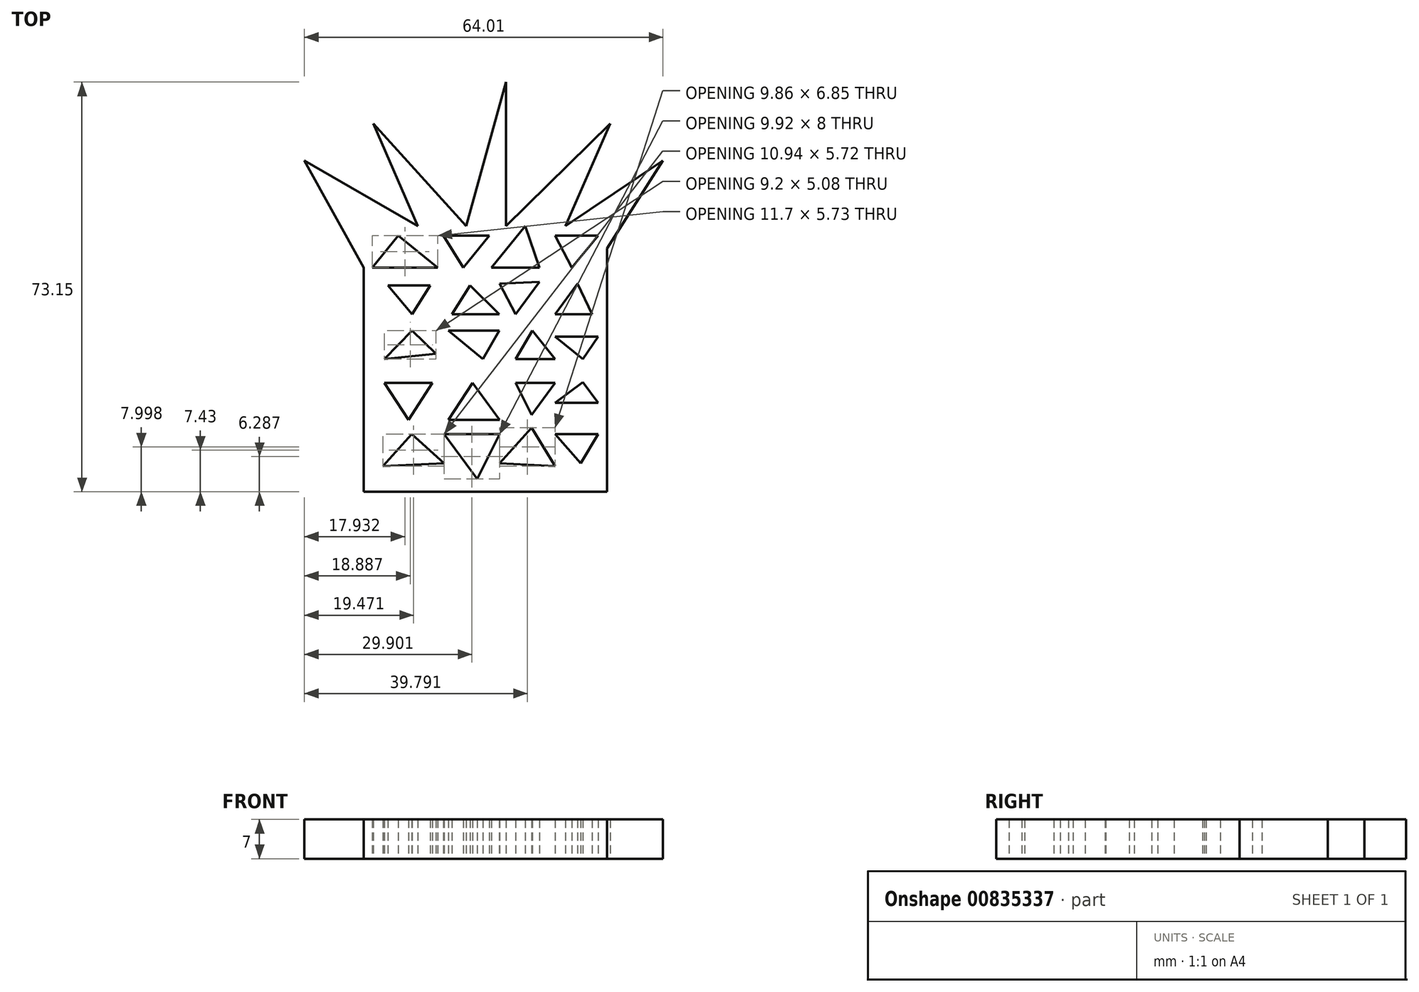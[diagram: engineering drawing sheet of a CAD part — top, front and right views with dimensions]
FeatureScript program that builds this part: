
annotation { "Feature Type Name" : "Feature", "Feature Type Description" : "" }
export const myFeature = defineFeature(function(context is Context, id is Id, definition is map)
    precondition{}
    {
        {
            var Q0;
            Q0=qCreatedBy(makeId("Top.planeOp"),FACE);
            var sketch = newSketch(context, id + "F0", { "sketchPlane" : qUnion([Q0])});
            skLineSegment(sketch, "E0.top", {"start": v(-34.1, -15.86) * mm, "end": v(9.29, -15.86) * mm});
            skLineSegment(sketch, "E0.left", {"start": v(-34.1, 24.13) * mm, "end": v(-34.1, -15.86) * mm});
            skLineSegment(sketch, "E0.right", {"start": v(9.29, 27.44) * mm, "end": v(9.29, -15.86) * mm});
            skLineSegment(sketch, "E1", {"start": v(9.29, 27.57) * mm, "end": v(19.29, 43.3) * mm});
            skLineSegment(sketch, "E2", {"start": v(19.29, 43.3) * mm, "end": v(1.9, 31.58) * mm});
            skLineSegment(sketch, "E3", {"start": v(1.9, 31.58) * mm, "end": v(9.86, 49.86) * mm});
            skLineSegment(sketch, "E4", {"start": v(9.86, 49.86) * mm, "end": v(-8.72, 31.58) * mm});
            skLineSegment(sketch, "E5", {"start": v(-8.72, 31.58) * mm, "end": v(-8.72, 57.3) * mm});
            skLineSegment(sketch, "E6", {"start": v(-8.72, 57.3) * mm, "end": v(-15.87, 31.58) * mm});
            skLineSegment(sketch, "E7", {"start": v(-15.87, 31.58) * mm, "end": v(-32.43, 49.86) * mm});
            skLineSegment(sketch, "E8", {"start": v(-32.43, 49.86) * mm, "end": v(-24.47, 31.58) * mm});
            skLineSegment(sketch, "E9", {"start": v(-24.47, 31.58) * mm, "end": v(-44.72, 43.3) * mm});
            skLineSegment(sketch, "E10", {"start": v(-44.72, 43.3) * mm, "end": v(-34.1, 24.13) * mm});
            skLineSegment(sketch, "E11", {"start": v(-15.87, 31.58) * mm, "end": v(-15.87, 31.58) * mm});
            skLineSegment(sketch, "E12", {"start": v(-32.64, 24.13) * mm, "end": v(-27.99, 29.86) * mm});
            skLineSegment(sketch, "E13", {"start": v(-27.99, 29.86) * mm, "end": v(-20.94, 24.13) * mm});
            skLineSegment(sketch, "E14", {"start": v(-20.94, 24.13) * mm, "end": v(-32.64, 24.13) * mm});
            skLineSegment(sketch, "E15", {"start": v(-19.93, 29.86) * mm, "end": v(-16.37, 24.13) * mm});
            skLineSegment(sketch, "E16", {"start": v(-16.37, 24.13) * mm, "end": v(-11.72, 29.86) * mm});
            skLineSegment(sketch, "E17", {"start": v(-11.72, 29.86) * mm, "end": v(-19.93, 29.86) * mm});
            skLineSegment(sketch, "E18", {"start": v(-11.33, 24.13) * mm, "end": v(-5.29, 31.58) * mm});
            skLineSegment(sketch, "E19", {"start": v(-5.29, 31.58) * mm, "end": v(-2.78, 24.13) * mm});
            skLineSegment(sketch, "E20", {"start": v(-11.33, 24.13) * mm, "end": v(-2.78, 24.13) * mm});
            skLineSegment(sketch, "E21", {"start": v(0, 29.86) * mm, "end": v(3.02, 24.13) * mm});
            skLineSegment(sketch, "E22", {"start": v(-29.8, 20.96) * mm, "end": v(-22.23, 20.96) * mm});
            skLineSegment(sketch, "E23", {"start": v(-22.23, 20.96) * mm, "end": v(-25.48, 15.86) * mm});
            skLineSegment(sketch, "E24", {"start": v(-29.8, 20.96) * mm, "end": v(-25.48, 15.86) * mm});
            skLineSegment(sketch, "E25", {"start": v(-18.4, 15.86) * mm, "end": v(-15.16, 20.96) * mm});
            skLineSegment(sketch, "E26", {"start": v(-15.16, 20.96) * mm, "end": v(-9.94, 15.86) * mm});
            skLineSegment(sketch, "E27", {"start": v(-18.4, 15.86) * mm, "end": v(-9.94, 15.86) * mm});
            skLineSegment(sketch, "E28", {"start": v(-9.86, 21.29) * mm, "end": v(-7, 15.86) * mm});
            skLineSegment(sketch, "E29", {"start": v(-2.78, 21.58) * mm, "end": v(-7, 15.86) * mm});
            skLineSegment(sketch, "E30", {"start": v(-2.78, 21.58) * mm, "end": v(-9.86, 21.29) * mm});
            skLineSegment(sketch, "E31", {"start": v(0, 15.86) * mm, "end": v(4, 21.29) * mm});
            skLineSegment(sketch, "E32", {"start": v(0, 15.86) * mm, "end": v(6.64, 15.86) * mm});
            skPoint(sketch, "E32.endSnap0", {"position": v(6.64, 18.7) * mm});
            skLineSegment(sketch, "E33", {"start": v(-30.43, 7.86) * mm, "end": v(-25.48, 12.93) * mm});
            skPoint(sketch, "E33.startSnap0", {"position": v(-34.1, 7.86) * mm});
            skLineSegment(sketch, "E34", {"start": v(-25.48, 12.93) * mm, "end": v(-21.23, 8.8) * mm});
            skLineSegment(sketch, "E35", {"start": v(-30.43, 7.86) * mm, "end": v(-21.23, 8.8) * mm});
            skLineSegment(sketch, "E36", {"start": v(-19, 12.93) * mm, "end": v(-9.94, 12.93) * mm});
            skLineSegment(sketch, "E37", {"start": v(-9.94, 12.93) * mm, "end": v(-12.87, 7.86) * mm});
            skLineSegment(sketch, "E38", {"start": v(-19, 12.93) * mm, "end": v(-12.87, 7.86) * mm});
            skLineSegment(sketch, "E39", {"start": v(-7, 7.86) * mm, "end": v(-4.06, 12.93) * mm});
            skLineSegment(sketch, "E40", {"start": v(-4.06, 12.93) * mm, "end": v(0, 7.86) * mm});
            skLineSegment(sketch, "E41", {"start": v(-7, 7.86) * mm, "end": v(0, 7.86) * mm});
            skPoint(sketch, "E42.endSnap0", {"position": v(9.29, 7.86) * mm});
            skLineSegment(sketch, "E43", {"start": v(0, 11.86) * mm, "end": v(5, 7.86) * mm});
            skLineSegment(sketch, "E44", {"start": v(-30.43, 3.57) * mm, "end": v(-21.86, 3.57) * mm});
            skLineSegment(sketch, "E45", {"start": v(-21.86, 3.57) * mm, "end": v(-26.15, -3) * mm});
            skLineSegment(sketch, "E46", {"start": v(-30.43, 3.57) * mm, "end": v(-26.15, -3) * mm});
            skLineSegment(sketch, "E47", {"start": v(-19, -3) * mm, "end": v(-14.72, 3.57) * mm});
            skLineSegment(sketch, "E48", {"start": v(-14.72, 3.57) * mm, "end": v(-9.86, -3) * mm});
            skLineSegment(sketch, "E49", {"start": v(-19, -3) * mm, "end": v(-9.86, -3) * mm});
            skLineSegment(sketch, "E50", {"start": v(-7, 3.57) * mm, "end": v(0, 3.57) * mm});
            skLineSegment(sketch, "E51", {"start": v(0, 3.57) * mm, "end": v(-4.14, -2.14) * mm});
            skLineSegment(sketch, "E52", {"start": v(-7, 3.57) * mm, "end": v(-4.14, -2.14) * mm});
            skLineSegment(sketch, "E53", {"start": v(0, 0) * mm, "end": v(5, 3.7) * mm});
            skLineSegment(sketch, "E54", {"start": v(-30.72, -11.29) * mm, "end": v(-25.57, -5.57) * mm});
            skLineSegment(sketch, "E55", {"start": v(-25.57, -5.57) * mm, "end": v(-19.78, -10.79) * mm});
            skLineSegment(sketch, "E56", {"start": v(-30.72, -11.29) * mm, "end": v(-19.78, -10.79) * mm});
            skLineSegment(sketch, "E57", {"start": v(-19.78, -5.57) * mm, "end": v(-9.86, -5.57) * mm});
            skLineSegment(sketch, "E58", {"start": v(-9.86, -5.57) * mm, "end": v(-13.86, -13.57) * mm});
            skLineSegment(sketch, "E59", {"start": v(-19.78, -5.57) * mm, "end": v(-13.86, -13.57) * mm});
            skLineSegment(sketch, "E60", {"start": v(-9.86, -10.79) * mm, "end": v(-4.14, -4.44) * mm});
            skLineSegment(sketch, "E61", {"start": v(-4.14, -4.44) * mm, "end": v(0, -11.29) * mm});
            skLineSegment(sketch, "E62", {"start": v(-9.86, -10.79) * mm, "end": v(0, -11.29) * mm});
            skLineSegment(sketch, "E63", {"start": v(4.6, -10.79) * mm, "end": v(0, -5.57) * mm});
            skLineSegment(sketch, "E64", {"start": v(5, 3.7) * mm, "end": v(7.73, 0) * mm});
            skLineSegment(sketch, "E65", {"start": v(7.73, 0) * mm, "end": v(0, 0) * mm});
            skLineSegment(sketch, "E66", {"start": v(0, -5.57) * mm, "end": v(7.73, -5.57) * mm});
            skLineSegment(sketch, "E67", {"start": v(7.73, -5.57) * mm, "end": v(4.6, -10.79) * mm});
            skLineSegment(sketch, "E68", {"start": v(4, 21.29) * mm, "end": v(6.64, 15.86) * mm});
            skLineSegment(sketch, "E69", {"start": v(0, 29.86) * mm, "end": v(7.73, 29.86) * mm});
            skLineSegment(sketch, "E70", {"start": v(7.73, 29.86) * mm, "end": v(3.02, 24.13) * mm});
            skLineSegment(sketch, "E71", {"start": v(0, 11.86) * mm, "end": v(7.73, 11.86) * mm});
            skLineSegment(sketch, "E72", {"start": v(7.73, 11.86) * mm, "end": v(5, 7.86) * mm});
            skLineSegment(sketch, "E73", {"start": v(9.29, 27.57) * mm, "end": v(9.29, -15.86) * mm});
            skSolve(sketch);
        }
        {
            var Q0;
            {var subQ0=sQuery(id+"F0.wireOp",EDGE,"E0.top");Q0=makeQuery(id+"F0.imprint","IMPRINT",FACE,{"disambiguationData":[TD([[makeQuery(id+"F0.imprint","IMPRINT",EDGE,{"derivedFrom":subQ0}),1.0]])]});}
            extrude(context, id + "F1", {"entities" : qUnion([Q0]), "depth" : 7 * mm, "offsetDistance" : 25.4 * mm});
        }
    });
